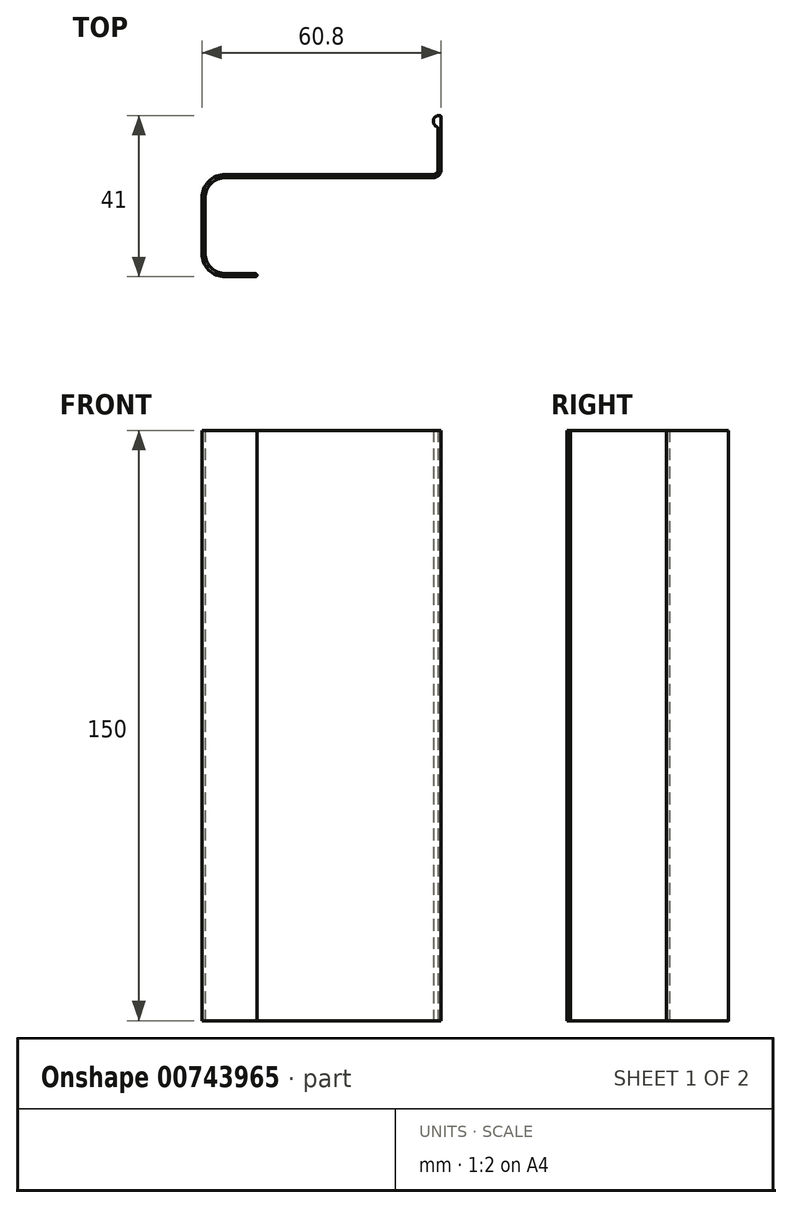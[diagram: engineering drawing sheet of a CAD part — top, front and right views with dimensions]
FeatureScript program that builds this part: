
annotation { "Feature Type Name" : "Feature", "Feature Type Description" : "" }
export const myFeature = defineFeature(function(context is Context, id is Id, definition is map)
    precondition{}
    {
        {
            var Q0;
            Q0=qCreatedBy(makeId("Top.planeOp"),FACE);
            var sketch = newSketch(context, id + "F0", { "sketchPlane" : qUnion([Q0])});
            skLineSegment(sketch, "E0", {"start": v(0, 6) * mm, "end": v(0, 20) * mm});
            skLineSegment(sketch, "E1", {"start": v(6, 26) * mm, "end": v(58.8, 26) * mm});
            skLineSegment(sketch, "E2", {"start": v(60, 27.2) * mm, "end": v(60, 37.67) * mm});
            skLineSegment(sketch, "E3", {"start": v(60.3, 41) * mm, "end": v(60.3, 41) * mm});
            skLineSegment(sketch, "E4", {"start": v(60.8, 40.5) * mm, "end": v(60.8, 27.2) * mm});
            skLineSegment(sketch, "E5", {"start": v(58.8, 25.2) * mm, "end": v(6, 25.2) * mm});
            skLineSegment(sketch, "E6", {"start": v(0.8, 20) * mm, "end": v(0.8, 6) * mm});
            skLineSegment(sketch, "E7", {"start": v(6, 0.8) * mm, "end": v(13.6, 0.8) * mm});
            skLineSegment(sketch, "E8", {"start": v(14, 0.4) * mm, "end": v(14, 0.4) * mm});
            skLineSegment(sketch, "E9", {"start": v(13.6, 0) * mm, "end": v(6, 0) * mm});
            skPoint(sketch, "E10.visualSharp", {"position": v(14, 0.8) * mm});
            skArc(sketch, "E10.filletArc", {"start": v(14, 0.4) * mm, "mid": v(13.88, 0.68) * mm, "end": v(13.6, 0.8) * mm});
            skPoint(sketch, "E11.visualSharp", {"position": v(14, 0) * mm});
            skArc(sketch, "E11.filletArc", {"start": v(13.6, 0) * mm, "mid": v(13.88, 0.12) * mm, "end": v(14, 0.4) * mm});
            skPoint(sketch, "E12.visualSharp", {"position": v(0, 0) * mm});
            skArc(sketch, "E12.filletArc", {"start": v(0, 6) * mm, "mid": v(1.76, 1.76) * mm, "end": v(6, 0) * mm});
            skPoint(sketch, "E13.visualSharp", {"position": v(0.8, 25.2) * mm});
            skArc(sketch, "E13.filletArc", {"start": v(6, 25.2) * mm, "mid": v(2.32, 23.68) * mm, "end": v(0.8, 20) * mm});
            skPoint(sketch, "E14.visualSharp", {"position": v(0.8, 0.8) * mm});
            skArc(sketch, "E14.filletArc", {"start": v(0.8, 6) * mm, "mid": v(2.32, 2.32) * mm, "end": v(6, 0.8) * mm});
            skPoint(sketch, "E15.visualSharp", {"position": v(0, 26) * mm});
            skArc(sketch, "E15.filletArc", {"start": v(6, 26) * mm, "mid": v(1.76, 24.24) * mm, "end": v(0, 20) * mm});
            skPoint(sketch, "E16.visualSharp", {"position": v(60.8, 25.2) * mm});
            skArc(sketch, "E16.filletArc", {"start": v(58.8, 25.2) * mm, "mid": v(60.21, 25.79) * mm, "end": v(60.8, 27.2) * mm});
            skPoint(sketch, "E17.visualSharp", {"position": v(60, 26) * mm});
            skArc(sketch, "E17.filletArc", {"start": v(58.8, 26) * mm, "mid": v(59.65, 26.35) * mm, "end": v(60, 27.2) * mm});
            skPoint(sketch, "E18.visualSharp", {"position": v(60, 41) * mm});
            skPoint(sketch, "E19.visualSharp", {"position": v(60.8, 41) * mm});
            skArc(sketch, "E19.filletArc", {"start": v(60.8, 40.5) * mm, "mid": v(60.65, 40.85) * mm, "end": v(60.3, 41) * mm});
            skArc(sketch, "E20", {"start": v(60.3, 41) * mm, "mid": v(58.83, 39.8) * mm, "end": v(59.7, 38.13) * mm});
            skPoint(sketch, "E21.visualSharp", {"position": v(60, 38.03) * mm});
            skArc(sketch, "E21.filletArc", {"start": v(60, 37.67) * mm, "mid": v(59.92, 37.94) * mm, "end": v(59.7, 38.13) * mm});
            skSolve(sketch);
        }
        {
            var Q0;
            Q0=makeQuery(id+"F0.imprint","IMPRINT",FACE,{"disambiguationData":[TD([[makeQuery(id+"F0.imprint","IMPRINT",EDGE,{"derivedFrom":sQuery(id+"F0.wireOp",EDGE,"E0")}),-1.0]])]});
            extrude(context, id + "F1", {"entities" : qUnion([Q0]), "depth" : 150 * mm, "offsetDistance" : 25 * mm});
        }
    });
